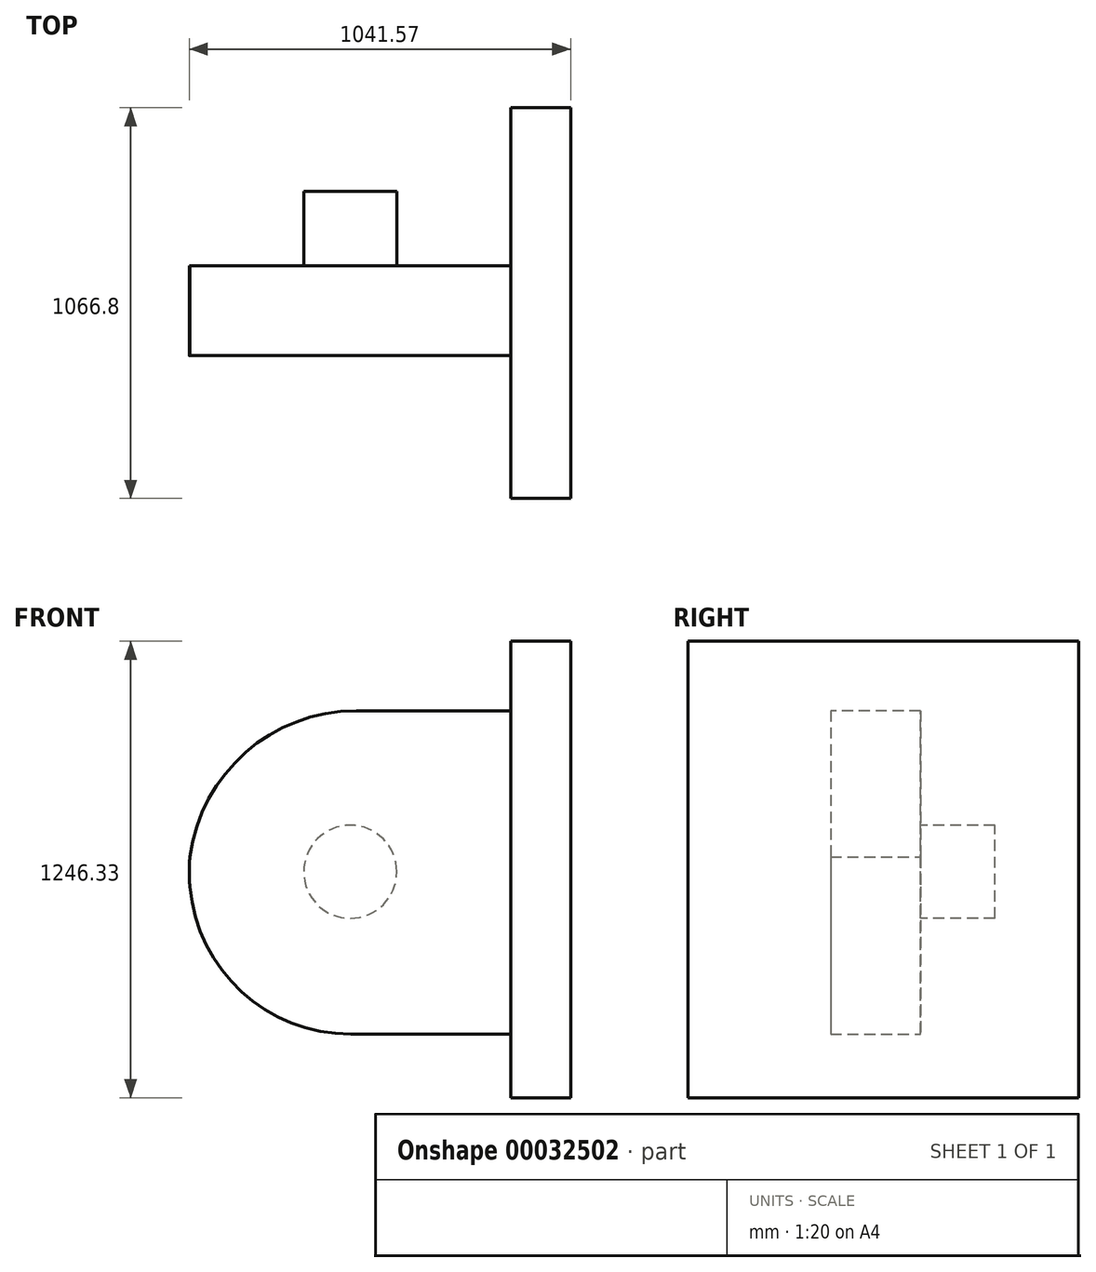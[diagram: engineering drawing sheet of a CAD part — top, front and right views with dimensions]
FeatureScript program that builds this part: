
annotation { "Feature Type Name" : "Feature", "Feature Type Description" : "" }
export const myFeature = defineFeature(function(context is Context, id is Id, definition is map)
    precondition{}
    {
        {
            var Q0;
            Q0=qCreatedBy(makeId("Front.planeOp"),FACE);
            var sketch = newSketch(context, id + "F0", { "sketchPlane" : qUnion([Q0])});
            skArc(sketch, "E0", {"start": v(-437.84, 40.39) * mm, "mid": v(-439.7, 0) * mm, "end": v(-437.84, -40.39) * mm});
            skCircle(sketch, "E1", {"center": v(0, 0) * mm, "radius": 127 * mm});
            skLineSegment(sketch, "E2.bottom", {"start": v(0, 439.7) * mm, "end": v(-437.84, 439.7) * mm});
            skLineSegment(sketch, "E2.top", {"start": v(0, -443.31) * mm, "end": v(-437.84, -443.31) * mm});
            skLineSegment(sketch, "E2.left", {"start": v(0, 439.7) * mm, "end": v(0, -443.31) * mm});
            skLineSegment(sketch, "E2.right", {"start": v(-437.84, 439.7) * mm, "end": v(-437.84, -443.31) * mm});
            skLineSegment(sketch, "E3.bottom", {"start": v(0, -443.31) * mm, "end": v(440.18, -443.31) * mm});
            skLineSegment(sketch, "E3.top", {"start": v(0, 439.7) * mm, "end": v(440.18, 439.7) * mm});
            skLineSegment(sketch, "E3.left", {"start": v(0, -443.31) * mm, "end": v(0, 439.7) * mm});
            skLineSegment(sketch, "E3.right", {"start": v(440.18, -443.31) * mm, "end": v(440.18, 439.7) * mm});
            skSolve(sketch);
        }
        {
            var Q0;
            Q0 = qSketchRegion(id + "F0", true);
            var Q1;
            Q1=makeQuery(id+"F0.imprint","IMPRINT",FACE,{"disambiguationData":[TD([[makeQuery(id+"F0.imprint","IMPRINT",EDGE,{"derivedFrom":sQuery(id+"F0.wireOp",EDGE,"E1")}),1.0]])]});
            extrude(context, id + "F1", {"entities" : qUnion([Q0, Q1]), "depth" : 245.37 * mm});
        }
        {
            var Q0;
            Q0=makeQuery(id+"F0.imprint","IMPRINT",FACE,{"disambiguationData":[TD([[makeQuery(id+"F0.imprint","IMPRINT",EDGE,{"derivedFrom":sQuery(id+"F0.wireOp",EDGE,"E1")}),1.0]])]});
            extrude(context, id + "F2", {"entities" : qUnion([Q0]), "operationType" : NewBodyOperationType.ADD, "oppositeDirection" : true, "depth" : 203.2 * mm});
        }
        {
            var Q0;
            Q0=qCreatedBy(makeId("Front.planeOp"),FACE);
            var sketch = newSketch(context, id + "F3", { "sketchPlane" : qUnion([Q0])});
            skLineSegment(sketch, "E4.bottom", {"start": v(438.84, -616.84) * mm, "end": v(601.87, -616.84) * mm});
            skLineSegment(sketch, "E4.top", {"start": v(438.84, 629.49) * mm, "end": v(601.87, 629.49) * mm});
            skLineSegment(sketch, "E4.left", {"start": v(438.84, -616.84) * mm, "end": v(438.84, 629.49) * mm});
            skLineSegment(sketch, "E4.right", {"start": v(601.87, -616.84) * mm, "end": v(601.87, 629.49) * mm});
            skSolve(sketch);
        }
        {
            var Q0;
            Q0 = qSketchRegion(id + "F3", true);
            extrude(context, id + "F4", {"entities" : qUnion([Q0]), "operationType" : NewBodyOperationType.ADD, "depth" : 635 * mm});
        }
        {
            var Q0;
            Q0 = qSketchRegion(id + "F3", true);
            extrude(context, id + "F5", {"entities" : qUnion([Q0]), "operationType" : NewBodyOperationType.ADD, "oppositeDirection" : true, "depth" : 431.8 * mm});
        }
        {
            var Q0;
            Q0=makeQuery(id+"F1.opExtrude","SWEPT_EDGE",EDGE,{"disambiguationData":[OSD([sQuery(id+"F0.wireOp",EDGE,"E2.bottom"),sQuery(id+"F0.wireOp",EDGE,"E2.right")])]});
            fillet(context, id + "F6", {"entities" : qUnion([Q0]), "radius" : 458 * mm, "tangentPropagation" : true, "allowEdgeOverflow" : false});
        }
        {
            var Q0;
            Q0=makeQuery(id+"F1.opExtrude","SWEPT_EDGE",EDGE,{"disambiguationData":[OSD([sQuery(id+"F0.wireOp",EDGE,"E2.top"),sQuery(id+"F0.wireOp",EDGE,"E2.right")])]});
            fillet(context, id + "F7", {"entities" : qUnion([Q0]), "radius" : 440.88 * mm, "tangentPropagation" : true, "allowEdgeOverflow" : false});
        }
    });
